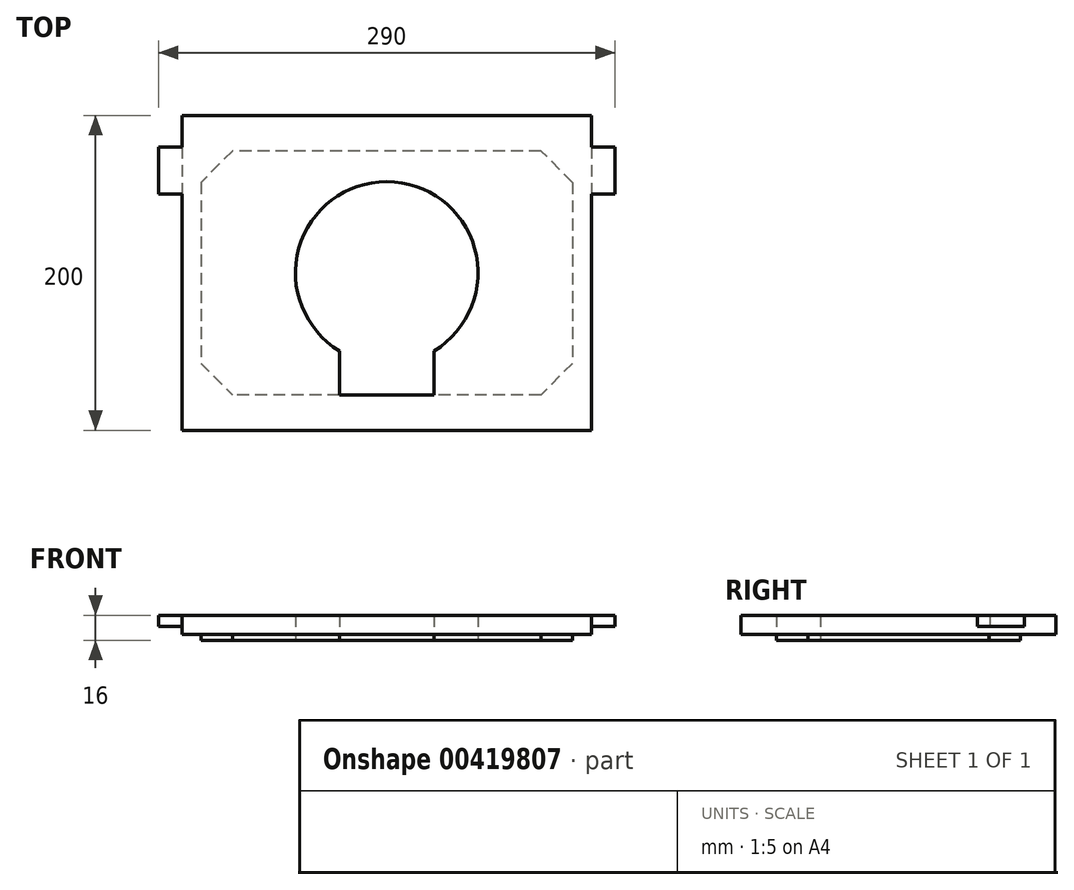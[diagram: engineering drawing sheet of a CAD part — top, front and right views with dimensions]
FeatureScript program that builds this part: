
annotation { "Feature Type Name" : "Feature", "Feature Type Description" : "" }
export const myFeature = defineFeature(function(context is Context, id is Id, definition is map)
    precondition{}
    {
        {
            var Q0;
            Q0=qCreatedBy(makeId("Top.planeOp"),FACE);
            var sketch = newSketch(context, id + "F0", { "sketchPlane" : qUnion([Q0])});
            skLineSegment(sketch, "E0.bottom", {"start": v(98, 77.5) * mm, "end": v(-98, 77.5) * mm});
            skLineSegment(sketch, "E0.top", {"start": v(98, -77.5) * mm, "end": v(30, -77.5) * mm});
            skLineSegment(sketch, "E0.left", {"start": v(118, 57.5) * mm, "end": v(118, -57.5) * mm});
            skLineSegment(sketch, "E0.right", {"start": v(-118, 57.5) * mm, "end": v(-118, -57.5) * mm});
            skPoint(sketch, "E0.middle", {"position": v(0, 0) * mm});
            skArc(sketch, "E1", {"start": v(30, -49.64) * mm, "mid": v(0, 58) * mm, "end": v(-30, -49.64) * mm});
            skLineSegment(sketch, "E2", {"start": v(-98, 77.5) * mm, "end": v(-118, 57.5) * mm});
            skLineSegment(sketch, "E3", {"start": v(-118, -57.5) * mm, "end": v(-98, -77.5) * mm});
            skLineSegment(sketch, "E4", {"start": v(118, -57.5) * mm, "end": v(98, -77.5) * mm});
            skLineSegment(sketch, "E5", {"start": v(118, 57.5) * mm, "end": v(98, 77.5) * mm});
            skPoint(sketch, "E6.orphan", {"position": v(-118, 77.5) * mm});
            skPoint(sketch, "E7.orphan", {"position": v(-118, -77.5) * mm});
            skPoint(sketch, "E8.orphan", {"position": v(118, -77.5) * mm});
            skPoint(sketch, "E9.orphan", {"position": v(118, 77.5) * mm});
            skPoint(sketch, "E10", {"position": v(-118, 0) * mm});
            skPoint(sketch, "E11", {"position": v(0, 77.5) * mm});
            skPoint(sketch, "E12", {"position": v(118, 0) * mm});
            skPoint(sketch, "E13", {"position": v(0, -77.5) * mm});
            skLineSegment(sketch, "E14", {"start": v(-30, -49.64) * mm, "end": v(-30, -77.5) * mm});
            skLineSegment(sketch, "E15", {"start": v(30, -49.64) * mm, "end": v(30, -77.5) * mm});
            skLineSegment(sketch, "E16.trimOffspring", {"start": v(-30, -77.5) * mm, "end": v(-98, -77.5) * mm});
            skLineSegment(sketch, "E17", {"start": v(-30, -77.5) * mm, "end": v(30, -77.5) * mm});
            skLineSegment(sketch, "E18.bottom", {"start": v(130, 100) * mm, "end": v(-130, 100) * mm});
            skLineSegment(sketch, "E18.top", {"start": v(130, -100) * mm, "end": v(-130, -100) * mm});
            skLineSegment(sketch, "E18.left", {"start": v(130, 100) * mm, "end": v(130, -100) * mm});
            skLineSegment(sketch, "E18.right", {"start": v(-130, 100) * mm, "end": v(-130, -100) * mm});
            skSolve(sketch);
        }
        {
            var Q0;
            Q0=makeQuery(id+"F0.imprint","IMPRINT",FACE,{"disambiguationData":[TD([[makeQuery(id+"F0.imprint","IMPRINT",EDGE,{"derivedFrom":sQuery(id+"F0.wireOp",EDGE,"E0.bottom")}),-1.0]])]});
            var Q1;
            Q1=makeQuery(id+"F0.imprint","IMPRINT",FACE,{"disambiguationData":[TD([[makeQuery(id+"F0.imprint","IMPRINT",EDGE,{"derivedFrom":sQuery(id+"F0.wireOp",EDGE,"E0.bottom")}),1.0]])]});
            extrude(context, id + "F1", {"entities" : qUnion([Q0, Q1]), "depth" : 12 * mm});
        }
        {
            var Q0;
            Q0=makeQuery(id+"F0.imprint","IMPRINT",FACE,{"disambiguationData":[TD([[makeQuery(id+"F0.imprint","IMPRINT",EDGE,{"derivedFrom":sQuery(id+"F0.wireOp",EDGE,"E0.bottom")}),1.0]])]});
            extrude(context, id + "F2", {"entities" : qUnion([Q0]), "operationType" : NewBodyOperationType.ADD, "oppositeDirection" : true, "depth" : 4 * mm});
        }
        {
            var Q0;
            Q0=makeQuery(id+"F1.opExtrude","CAP_FACE",FACE,{"disambiguationData":[OSD([sQuery(id+"F0.wireOp",EDGE,"E1"),sQuery(id+"F0.wireOp",EDGE,"E14"),sQuery(id+"F0.wireOp",EDGE,"E15"),sQuery(id+"F0.wireOp",EDGE,"E17"),sQuery(id+"F0.wireOp",EDGE,"E18.bottom"),sQuery(id+"F0.wireOp",EDGE,"E18.top"),sQuery(id+"F0.wireOp",EDGE,"E18.left"),sQuery(id+"F0.wireOp",EDGE,"E18.right")])],"isStart":false});
            var sketch = newSketch(context, id + "F3", { "sketchPlane" : qUnion([Q0])});
            skLineSegment(sketch, "E19.bottom", {"start": v(-130, 80) * mm, "end": v(-145, 80) * mm});
            skLineSegment(sketch, "E19.top", {"start": v(-130, 50) * mm, "end": v(-145, 50) * mm});
            skLineSegment(sketch, "E19.left", {"start": v(-130, 80) * mm, "end": v(-130, 50) * mm});
            skLineSegment(sketch, "E19.right", {"start": v(-145, 80) * mm, "end": v(-145, 50) * mm});
            skLineSegment(sketch, "E20", {"start": v(0, 58) * mm, "end": v(0, -77.5) * mm, "construction": true});
            skLineSegment(sketch, "E21.MirrorCS", {"start": v(130, 50) * mm, "end": v(145, 50) * mm});
            skLineSegment(sketch, "E22.MirrorCS", {"start": v(130, 80) * mm, "end": v(130, 50) * mm});
            skLineSegment(sketch, "E23.MirrorCS", {"start": v(130, 80) * mm, "end": v(145, 80) * mm});
            skLineSegment(sketch, "E24.MirrorCS", {"start": v(145, 80) * mm, "end": v(145, 50) * mm});
            skSolve(sketch);
        }
        {
            var Q0;
            Q0=makeQuery(id+"F3.imprint","IMPRINT",FACE,{"disambiguationData":[TD([[makeQuery(id+"F3.imprint","IMPRINT",EDGE,{"derivedFrom":sQuery(id+"F3.wireOp",EDGE,"E19.bottom")}),1.0]])]});
            var Q1;
            Q1=makeQuery(id+"F3.imprint","IMPRINT",FACE,{"disambiguationData":[TD([[makeQuery(id+"F3.imprint","IMPRINT",EDGE,{"derivedFrom":sQuery(id+"F3.wireOp",EDGE,"E21.MirrorCS")}),1.0]])]});
            extrude(context, id + "F4", {"entities" : qUnion([Q0, Q1]), "operationType" : NewBodyOperationType.ADD, "oppositeDirection" : true, "depth" : 7 * mm});
        }
    });
